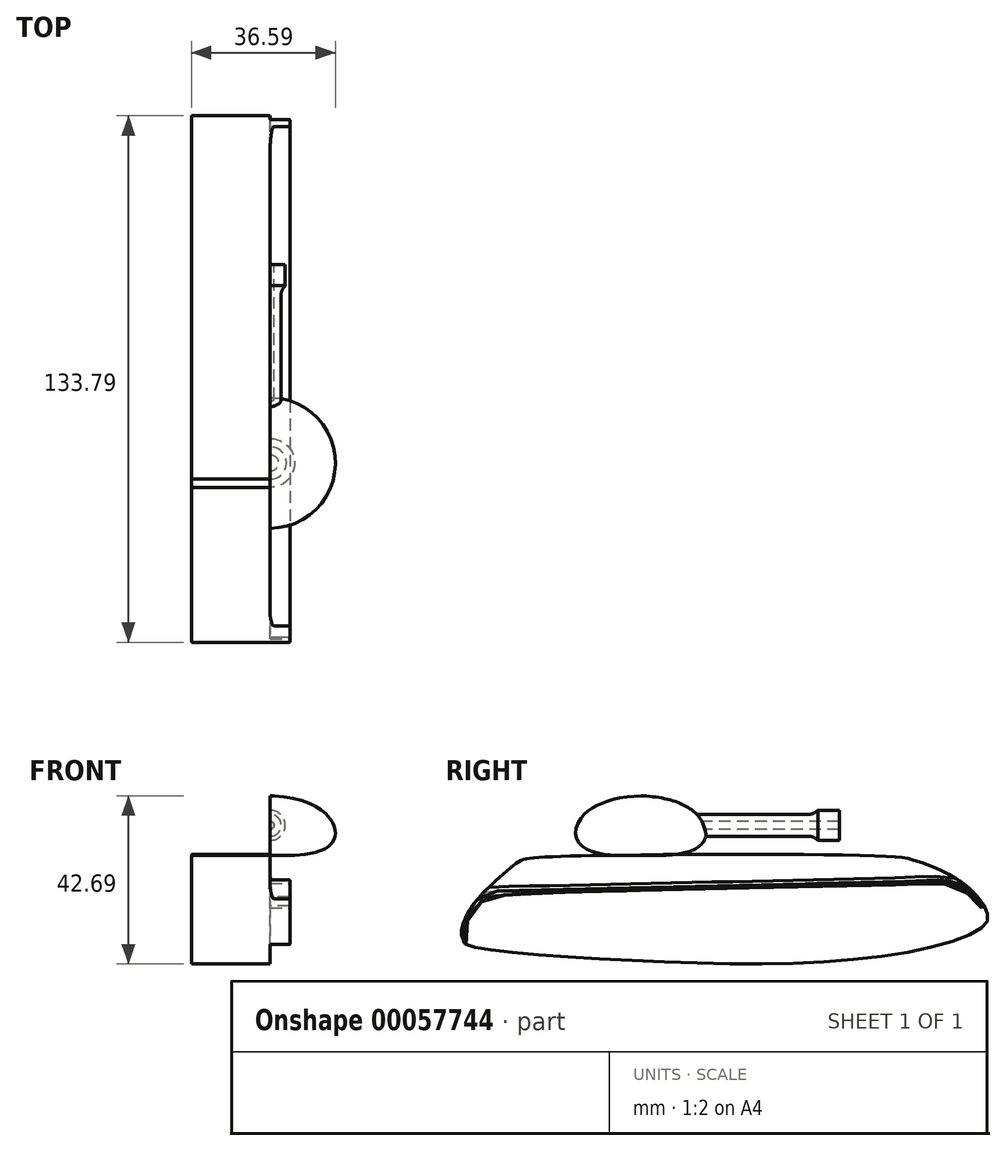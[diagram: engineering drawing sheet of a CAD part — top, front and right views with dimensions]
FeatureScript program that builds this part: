
annotation { "Feature Type Name" : "Feature", "Feature Type Description" : "" }
export const myFeature = defineFeature(function(context is Context, id is Id, definition is map)
    precondition{}
    {
        {
            var Q0;
            Q0=qCreatedBy(makeId("Right.planeOp"),FACE);
            var sketch = newSketch(context, id + "F0", { "sketchPlane" : qUnion([Q0])});
            skCircle(sketch, "E0", {"center": v(-28.96, -3.17) * mm, "radius": 5 * mm});
            skCircle(sketch, "E1", {"center": v(-2.58, -4.3) * mm, "radius": 5 * mm});
            skCircle(sketch, "E2", {"center": v(39.7, -1.22) * mm, "radius": 5 * mm});
            skCircle(sketch, "E3", {"center": v(-18.18, -4.4) * mm, "radius": 5 * mm});
            skCircle(sketch, "E4", {"center": v(-10.3, -4.22) * mm, "radius": 5 * mm});
            skCircle(sketch, "E5", {"center": v(5.45, -4.3) * mm, "radius": 5 * mm});
            skCircle(sketch, "E6", {"center": v(13.65, -4.38) * mm, "radius": 5 * mm});
            skCircle(sketch, "E7", {"center": v(21.76, -4.3) * mm, "radius": 5 * mm});
            skCircle(sketch, "E8", {"center": v(30, -3.33) * mm, "radius": 5 * mm});
            skCircle(sketch, "E9", {"center": v(-23.68, -3.72) * mm, "radius": 5 * mm});
            skFitSpline(sketch, "E10", {"points": [v(-24.17, -9.89) * mm, v(-31.03, -7.92) * mm, v(-32.53, -6.92) * mm, v(-33.27, -6.1) * mm, v(-33.97, -4.52) * mm, v(-34.12, -2.96) * mm, v(-33.94, -1.56) * mm, v(-32.9, 0.38) * mm, v(-30.87, 1.84) * mm, v(-29.21, 2.25) * mm, v(-21.63, 2.4) * mm, v(-13.26, 2.7) * mm, v(0.23, 3.13) * mm, v(12.27, 3.48) * mm, v(21.47, 3.78) * mm, v(33.09, 4.1) * mm, v(40.9, 4.3) * mm, v(43.62, 3.13) * mm, v(44.92, 1.76) * mm, v(45.6, 0.14) * mm, v(45.77, -1.5) * mm, v(45.48, -3) * mm, v(44.3, -5.04) * mm, v(42.31, -6.55) * mm, v(39.76, -7.29) * mm, v(33.79, -9.01) * mm, v(30.2, -9.88) * mm, v(27.4, -9.9) * mm, v(15.87, -9.91) * mm, v(8.9, -9.95) * mm, v(0.58, -9.94) * mm, v(-6.07, -9.92) * mm, v(-23.25, -9.9) * mm, v(-24, -9.9) * mm, v(-24.17, -9.89) * mm]});
            skFitSpline(sketch, "E11", {"points": [v(36.24, 2.39) * mm, v(-29.3, 0.64) * mm, v(-31.26, -0.5) * mm, v(-31.92, -1.76) * mm, v(-32.1, -3.51) * mm, v(-31.2, -5.66) * mm, v(-24.35, -8.14) * mm, v(-14.07, -8.25) * mm, v(26.48, -8.3) * mm, v(38.18, -5.98) * mm], "startDerivative": vector(-329.05, -3.13) * mm, "endDerivative": vector(74.4, 23.16) * mm});
            skSolve(sketch);
        }
        {
            var Q0;
            Q0=qCreatedBy(makeId("Right.planeOp"),FACE);
            var sketch = newSketch(context, id + "F1", { "sketchPlane" : qUnion([Q0])});
            skFitSpline(sketch, "E12", {"points": [v(59.07, 13.45) * mm, v(69.37, 8.54) * mm, v(75.89, 1.47) * mm, v(75.78, -2.32) * mm, v(50.58, -10.36) * mm, v(-18.72, -11.34) * mm, v(-56.13, -7.54) * mm, v(-56.76, -6.63) * mm, v(-57.35, -4.31) * mm, v(-55.94, 0) * mm, v(-53.19, 4.08) * mm, v(-43.95, 12.67) * mm, v(-37.22, 14.65) * mm, v(49.13, 14.97) * mm, v(59.07, 13.45) * mm]});
            skFitSpline(sketch, "E13", {"points": [v(-56.13, -7.54) * mm, v(-56.32, -5.68) * mm, v(-56.13, -2.34) * mm, v(-53.65, 2.1) * mm, v(-51.23, 4.01) * mm, v(-46.61, 5) * mm, v(59.02, 7.83) * mm, v(63.02, 8) * mm, v(66.47, 7.78) * mm, v(69, 6.85) * mm, v(73, 3.72) * mm, v(74.64, 1.8) * mm, v(75.47, 2.25) * mm], "startDerivative": vector(20.98, 23.71) * mm, "endDerivative": vector(29.62, 12.52) * mm});
            skFitSpline(sketch, "E14", {"points": [v(-53.19, 4.08) * mm, v(-50.43, 5.92) * mm, v(-46.7, 6.18) * mm, v(58.95, 8.66) * mm, v(62.83, 8.83) * mm, v(66.61, 8.66) * mm, v(69.35, 7.74) * mm, v(73.73, 4.64) * mm], "startDerivative": vector(59.6, 46.87) * mm, "endDerivative": vector(42, -39.14) * mm});
            skLineSegment(sketch, "E15", {"start": v(-11.78, 15.27) * mm, "end": v(-11.78, 41.69) * mm, "construction": true});
            skFitSpline(sketch, "E16", {"points": [v(-13.88, 15.24) * mm, v(-18.58, 15.2) * mm, v(-23.46, 15.92) * mm, v(-26.84, 17.61) * mm, v(-28.34, 20.22) * mm, v(-27.55, 23.67) * mm, v(-25.23, 26.3) * mm, v(-22.24, 28.12) * mm, v(-18.15, 29.48) * mm, v(-11.78, 30.27) * mm], "startDerivative": vector(-41.95, 0.4) * mm, "endDerivative": vector(39.1, 1.03) * mm});
            skLineSegment(sketch, "E17", {"start": v(-11.78, 15.27) * mm, "end": v(-11.78, 30.27) * mm});
            skLineSegment(sketch, "E18", {"start": v(-11.78, 22.77) * mm, "end": v(89.65, 22.77) * mm});
            skLineSegment(sketch, "E19", {"start": v(-11.78, 19.97) * mm, "end": v(33.22, 19.97) * mm});
            skLineSegment(sketch, "E20", {"start": v(33.22, 19.97) * mm, "end": v(33.22, 18.92) * mm});
            skLineSegment(sketch, "E21", {"start": v(33.22, 18.92) * mm, "end": v(38.63, 18.92) * mm});
            skLineSegment(sketch, "E22", {"start": v(38.63, 18.92) * mm, "end": v(38.63, 22.77) * mm});
            skLineSegment(sketch, "E23", {"start": v(38.63, 21.77) * mm, "end": v(-11.78, 21.77) * mm});
            skSolve(sketch);
        }
        {
            var Q0;
            {var subQ4=sQuery(id+"F1.wireOp",EDGE,"E17");Q0=makeQuery(id+"F1.imprint","IMPRINT",FACE,{"disambiguationData":[TD([[makeQuery(id+"F1.imprint","IMPRINT",EDGE,{"derivedFrom":subQ4}),1.0]])]});}
            var Q1;
            Q1=sQuery(id+"F1.wireOp",EDGE,"E15");
            revolve(context, id + "F2", {"entities" : qUnion([Q0]), "axis" : qUnion([Q1]), "revolveType" : RevolveType.ONE_DIRECTION, "angle" : 180 * degree});
        }
        {
            var Q0;
            {var subQ0=sQuery(id+"F1.wireOp",EDGE,"E19");Q0=makeQuery(id+"F1.imprint","IMPRINT",FACE,{"disambiguationData":[TD([[makeQuery(id+"F1.imprint","IMPRINT",EDGE,{"derivedFrom":subQ0}),1.0]])]});}
            var Q1;
            Q1=sQuery(id+"F1.wireOp",EDGE,"E18");
            revolve(context, id + "F3", {"operationType" : NewBodyOperationType.ADD, "entities" : qUnion([Q0]), "axis" : qUnion([Q1]), "revolveType" : RevolveType.ONE_DIRECTION, "oppositeDirection" : true, "angle" : 180 * degree});
        }
        {
            var Q0;
            Q0=makeQuery(id+"F3.opRevolve","SWEPT_EDGE",EDGE,{"disambiguationData":[OSD([sQuery(id+"F1.wireOp",EDGE,"E19"),sQuery(id+"F1.wireOp",EDGE,"E20")])]});
            fillet(context, id + "F4", {"entities" : qUnion([Q0]), "radius" : 3 * mm, "tangentPropagation" : true, "allowEdgeOverflow" : false});
        }
        {
            var Q0;
            {var subQ0=sQuery(id+"F1.wireOp",EDGE,"E14");Q0=makeQuery(id+"F1.imprint","IMPRINT",FACE,{"disambiguationData":[TD([[makeQuery(id+"F1.imprint","IMPRINT",EDGE,{"derivedFrom":subQ0}),1.0]])]});}
            var Q1;
            {var subQ0=sQuery(id+"F1.wireOp",EDGE,"E13");Q1=makeQuery(id+"F1.imprint","IMPRINT",FACE,{"disambiguationData":[TD([[makeQuery(id+"F1.imprint","IMPRINT",EDGE,{"derivedFrom":subQ0}),1.0]])]});}
            var Q2;
            {var subQ0=sQuery(id+"F1.wireOp",EDGE,"E13");Q2=makeQuery(id+"F1.imprint","IMPRINT",FACE,{"disambiguationData":[TD([[makeQuery(id+"F1.imprint","IMPRINT",EDGE,{"derivedFrom":subQ0}),-1.0]])]});}
            extrude(context, id + "F5", {"entities" : qUnion([Q0, Q1, Q2]), "oppositeDirection" : true, "depth" : 20 * mm});
        }
        {
            var Q0;
            {var subQ0=sQuery(id+"F1.wireOp",EDGE,"E13");Q0=makeQuery(id+"F1.imprint","IMPRINT",FACE,{"disambiguationData":[TD([[makeQuery(id+"F1.imprint","IMPRINT",EDGE,{"derivedFrom":subQ0}),1.0]])]});}
            extrude(context, id + "F6", {"entities" : qUnion([Q0]), "operationType" : NewBodyOperationType.ADD, "depth" : 5 * mm});
        }
        {
            var Q0;
            Q0=makeQuery(id+"F6.opExtrude","CAP_FACE",FACE,{"disambiguationData":[OSD([sQuery(id+"F1.wireOp",EDGE,"E12"),sQuery(id+"F1.wireOp",EDGE,"E13"),sQuery(id+"F1.wireOp",EDGE,"E14")])],"isStart":false});
            fillet(context, id + "F7", {"entities" : qUnion([Q0]), "radius" : .1 * mm, "tangentPropagation" : true, "allowEdgeOverflow" : false});
        }
        {
            var Q0;
            Q0=makeQuery(id+"F6.opExtrude","CAP_EDGE",EDGE,{"disambiguationData":[OSD([sQuery(id+"F1.wireOp",EDGE,"E14")])],"isStart":true});
            fillet(context, id + "F8", {"entities" : qUnion([Q0]), "radius" : 1 * mm, "tangentPropagation" : true, "allowEdgeOverflow" : false});
        }
    });
